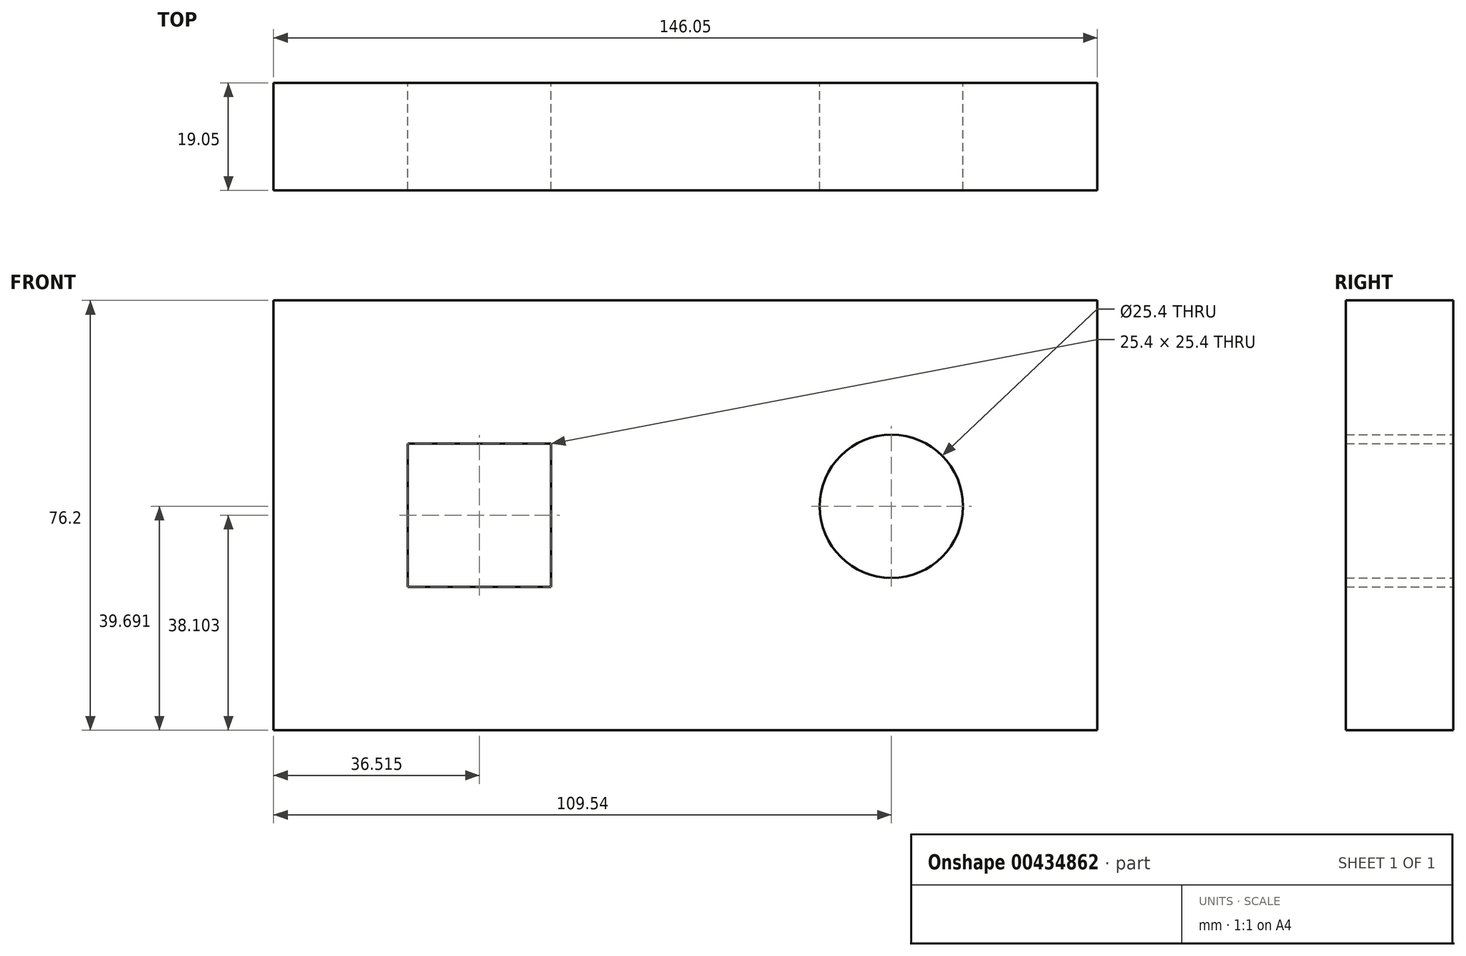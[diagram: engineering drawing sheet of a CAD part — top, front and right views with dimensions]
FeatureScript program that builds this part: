
annotation { "Feature Type Name" : "Feature", "Feature Type Description" : "" }
export const myFeature = defineFeature(function(context is Context, id is Id, definition is map)
    precondition{}
    {
        {
            var Q0;
            Q0=qCreatedBy(makeId("Front.planeOp"),FACE);
            var sketch = newSketch(context, id + "F0", { "sketchPlane" : qUnion([Q0])});
            skLineSegment(sketch, "E0.bottom", {"start": v(-77.5, 48.9) * mm, "end": v(68.55, 48.9) * mm});
            skLineSegment(sketch, "E0.top", {"start": v(-77.5, -27.3) * mm, "end": v(68.55, -27.3) * mm});
            skLineSegment(sketch, "E0.left", {"start": v(-77.5, 48.9) * mm, "end": v(-77.5, -27.3) * mm});
            skLineSegment(sketch, "E0.right", {"start": v(68.55, 48.9) * mm, "end": v(68.55, -27.3) * mm});
            skLineSegment(sketch, "E1.bottom", {"start": v(-53.68, 23.5) * mm, "end": v(-28.28, 23.5) * mm});
            skLineSegment(sketch, "E1.top", {"start": v(-53.68, -1.9) * mm, "end": v(-28.28, -1.9) * mm});
            skLineSegment(sketch, "E1.left", {"start": v(-53.68, 23.5) * mm, "end": v(-53.68, -1.9) * mm});
            skLineSegment(sketch, "E1.right", {"start": v(-28.28, 23.5) * mm, "end": v(-28.28, -1.9) * mm});
            skCircle(sketch, "E2", {"center": v(32.04, 12.38) * mm, "radius": 12.7 * mm});
            skSolve(sketch);
        }
        {
            var Q0;
            Q0 = qSketchRegion(id + "F0", true);
            extrude(context, id + "F1", {"entities" : qUnion([Q0]), "depth" : 19.05 * mm});
        }
    });
